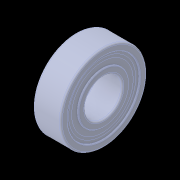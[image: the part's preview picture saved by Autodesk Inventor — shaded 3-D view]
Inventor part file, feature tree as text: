
AUTODESK INVENTOR PART (.ipt)
format: ipt  version: 2016 (Build 200138000, 138)  size: 200,192 bytes
history: native  units: in
note: dims shown in document units (in); Inventor stores cm internally (conversion verified against a paired STEP export)
features: revolve x1
ambient origin geometry x8: Origin, YZ Plane, XZ Plane, XY Plane, X Axis, Y Axis, Z Axis, Center Point
bodies: Solid1 (feature_tree)
feature tree (1):
  revolve  "Revolve1"  [1 undecoded]
note: 1 required parameter value undecoded (feature->parameter linkage not recoverable at this tier; creation-order binding heuristic only, values carry confidence <= 0.55)
